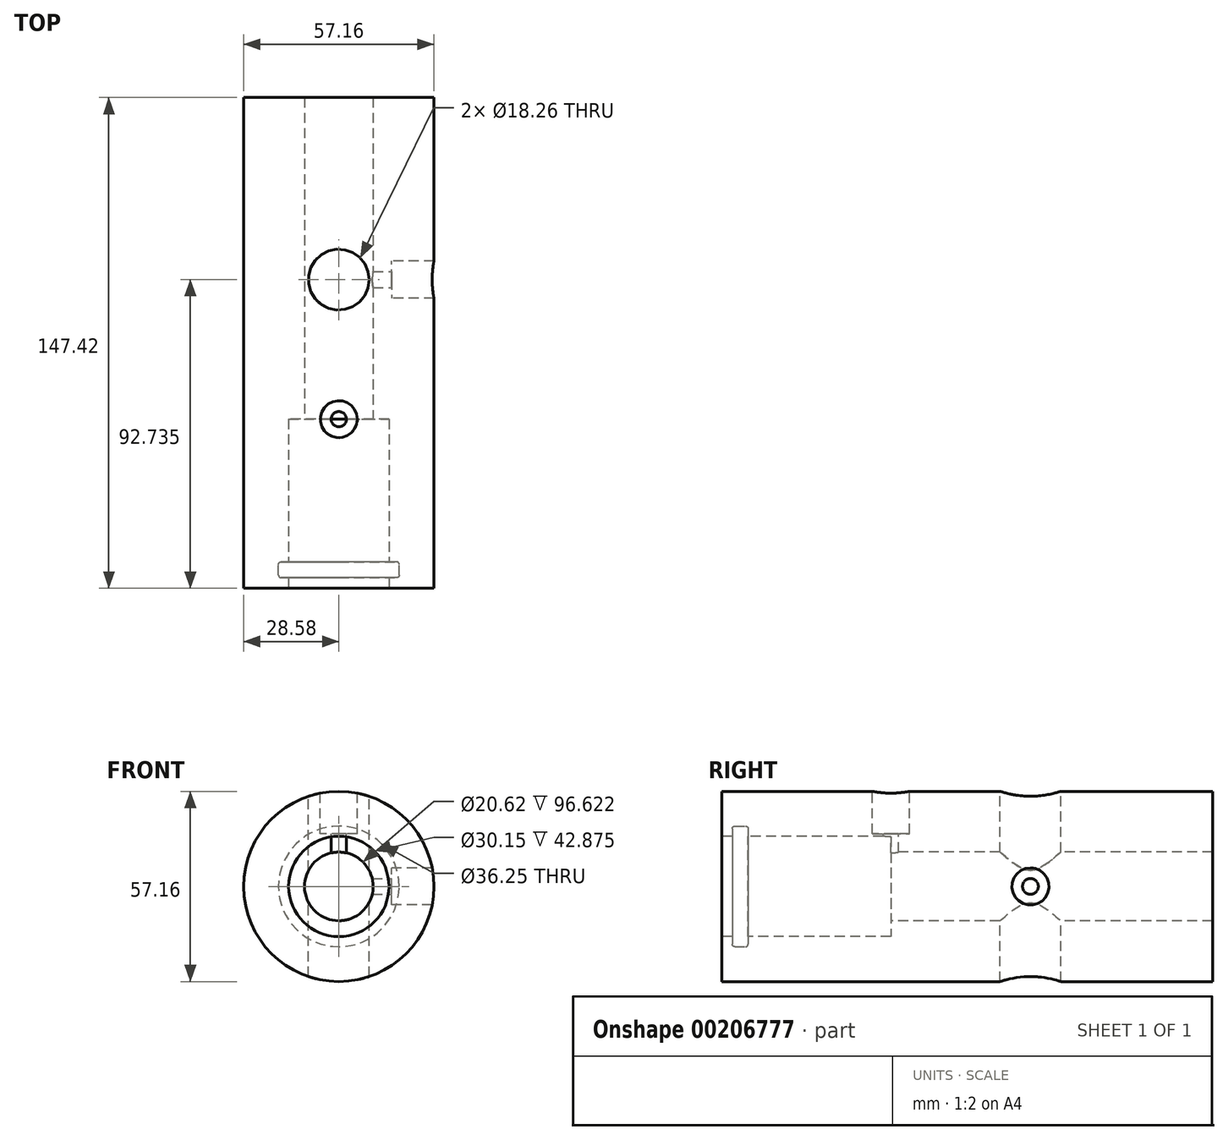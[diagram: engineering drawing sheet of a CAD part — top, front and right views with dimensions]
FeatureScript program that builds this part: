
annotation { "Feature Type Name" : "Feature", "Feature Type Description" : "" }
export const myFeature = defineFeature(function(context is Context, id is Id, definition is map)
    precondition{}
    {
        {
            var Q0;
            Q0=qCreatedBy(makeId("Front.planeOp"),FACE);
            var sketch = newSketch(context, id + "F0", { "sketchPlane" : qUnion([Q0])});
            skCircle(sketch, "E0", {"center": v(0, 0) * mm, "radius": 28.58 * mm});
            skSolve(sketch);
        }
        {
            var Q0;
            Q0=qSketchRegion(id+"F0",true);
            extrude(context, id + "F1", {"entities" : qUnion([Q0]), "oppositeDirection" : true, "depth" : 147.42 * mm});
        }
        {
            var Q0;
            Q0=makeQuery(id+"F1.opExtrude","CAP_FACE",FACE,{"disambiguationData":[OSD([sQuery(id+"F0.wireOp",EDGE,"E0")])],"isStart":true});
            var sketch = newSketch(context, id + "F2", { "sketchPlane" : qUnion([Q0])});
            skCircle(sketch, "E1", {"center": v(0, 0) * mm, "radius": 15.07 * mm});
            skCircle(sketch, "E2", {"center": v(0, 0) * mm, "radius": 10.31 * mm});
            skSolve(sketch);
        }
        {
            var Q0;
            Q0=makeQuery(id+"F2.imprint","IMPRINT",FACE,{"disambiguationData":[TD([[makeQuery(id+"F2.imprint","IMPRINT",EDGE,{"derivedFrom":sQuery(id+"F2.wireOp",EDGE,"E2")}),1.0]])]});
            extrude(context, id + "F3", {"entities" : qUnion([Q0]), "operationType" : NewBodyOperationType.REMOVE, "endBound" : BoundingType.THROUGH_ALL, "oppositeDirection" : true, "depth" : 25.4 * mm});
        }
        {
            var Q0;
            Q0=qSketchRegion(id+"F2",true);
            extrude(context, id + "F4", {"entities" : qUnion([Q0]), "operationType" : NewBodyOperationType.REMOVE, "oppositeDirection" : true, "depth" : 50.8 * mm});
        }
        {
            var Q0;
            Q0=qCreatedBy(makeId("Top.planeOp"),FACE);
            cPlane(context, id + "F5", {"entities" : qUnion([Q0]), "cplaneType" : CPlaneType.OFFSET, "offset" : 28.57 * mm, "width" : 152.4 * mm, "height" : 152.4 * mm});
        }
        {
            var Q0;
            Q0=qCreatedBy(id+"F5.planeOp",FACE);
            var sketch = newSketch(context, id + "F6", { "sketchPlane" : qUnion([Q0])});
            skCircle(sketch, "E3", {"center": v(0, 92.74) * mm, "radius": 9.13 * mm});
            skSolve(sketch);
        }
        {
            var Q0;
            Q0=qSketchRegion(id+"F6",true);
            var Q1;
            Q1=makeQuery(id+"F3.boolean.opBoolean","COPY",FACE,{"derivedFrom":makeQuery(id+"F3.opExtrude","SWEPT_FACE",FACE,{"disambiguationData":[OSD([sQuery(id+"F2.wireOp",EDGE,"E2")])]})});
            extrude(context, id + "F7", {"entities" : qUnion([Q0]), "operationType" : NewBodyOperationType.REMOVE, "endBound" : BoundingType.THROUGH_ALL, "oppositeDirection" : true, "endBoundEntityFace" : qUnion([Q1]), "depth" : 19.05 * mm});
        }
        {
            var Q0;
            Q0=qCreatedBy(makeId("Right.planeOp"),FACE);
            var sketch = newSketch(context, id + "F8", { "sketchPlane" : qUnion([Q0])});
            skLineSegment(sketch, "E4", {"start": v(0, 0) * mm, "end": v(50.8, 0) * mm, "construction": true});
            skLineSegment(sketch, "E5.bottom", {"start": v(3.17, 18.12) * mm, "end": v(7.92, 18.12) * mm});
            skLineSegment(sketch, "E5.top", {"start": v(3.17, 15.07) * mm, "end": v(7.92, 15.07) * mm});
            skLineSegment(sketch, "E5.left", {"start": v(3.17, 15.07) * mm, "end": v(3.17, 18.12) * mm});
            skLineSegment(sketch, "E5.right", {"start": v(7.92, 15.07) * mm, "end": v(7.92, 18.12) * mm});
            skSolve(sketch);
        }
        {
            var Q0;
            Q0=qSketchRegion(id+"F8",true);
            var Q1;
            Q1=sQuery(id+"F8.wireOp",EDGE,"E4");
            revolve(context, id + "F9", {"operationType" : NewBodyOperationType.REMOVE, "entities" : qUnion([Q0]), "axis" : qUnion([Q1]), "revolveType" : RevolveType.FULL, "oppositeDirection" : true});
        }
        {
            var Q0;
            Q0=qCreatedBy(id+"F5.planeOp",FACE);
            var sketch = newSketch(context, id + "F10", { "sketchPlane" : qUnion([Q0])});
            skCircle(sketch, "E6", {"center": v(0, 50.8) * mm, "radius": 5.56 * mm});
            skCircle(sketch, "E7", {"center": v(0, 50.8) * mm, "radius": 2.29 * mm});
            skSolve(sketch);
        }
        {
            var Q0;
            Q0=makeQuery(id+"F10.imprint","IMPRINT",FACE,{"disambiguationData":[TD([[makeQuery(id+"F10.imprint","IMPRINT",EDGE,{"derivedFrom":sQuery(id+"F10.wireOp",EDGE,"E7")}),1.0]])]});
            extrude(context, id + "F11", {"entities" : qUnion([Q0]), "operationType" : NewBodyOperationType.REMOVE, "endBound" : BoundingType.UP_TO_NEXT, "oppositeDirection" : true, "depth" : 25.4 * mm});
        }
        {
            var Q0;
            Q0=qSketchRegion(id+"F10",true);
            extrude(context, id + "F12", {"entities" : qUnion([Q0]), "operationType" : NewBodyOperationType.REMOVE, "oppositeDirection" : true, "depth" : 12.7 * mm});
        }
        {
            var Q0;
            Q0=qCreatedBy(makeId("Right.planeOp"),FACE);
            var sketch = newSketch(context, id + "F13", { "sketchPlane" : qUnion([Q0])});
            skLineSegment(sketch, "E8", {"start": v(92.74, 28.58) * mm, "end": v(92.74, 0) * mm, "construction": true});
            skCircle(sketch, "E9", {"center": v(92.74, 0) * mm, "radius": 5.56 * mm});
            skSolve(sketch);
        }
        {
            var Q0;
            Q0 = qSketchRegion(id + "F13", true);
            var Q1;
            Q1=makeQuery(id+"F1.opExtrude","SWEPT_FACE",FACE,{"disambiguationData":[OSD([sQuery(id+"F0.wireOp",EDGE,"E0")])]});
            extrude(context, id + "F14", {"entities" : qUnion([Q0]), "operationType" : NewBodyOperationType.REMOVE, "endBound" : BoundingType.UP_TO_SURFACE, "endBoundEntityFace" : qUnion([Q1]), "depth" : 25.4 * mm, "hasSecondDirection" : true, "secondDirectionOppositeDirection" : false, "secondDirectionDepth" : 15.88 * mm});
        }
        {
            var Q0;
            Q0=makeQuery(id+"F14.boolean.opBoolean","COPY",FACE,{"derivedFrom":makeQuery(id+"F14.opExtrude","CAP_FACE",FACE,{"disambiguationData":[OSD([sQuery(id+"F13.wireOp",EDGE,"E9")])],"isStart":true})});
            var sketch = newSketch(context, id + "F15", { "sketchPlane" : qUnion([Q0])});
            skCircle(sketch, "E10", {"center": v(92.74, 0) * mm, "radius": 2.38 * mm});
            skSolve(sketch);
        }
        {
            var Q0;
            Q0 = qSketchRegion(id + "F15", true);
            extrude(context, id + "F16", {"entities" : qUnion([Q0]), "operationType" : NewBodyOperationType.REMOVE, "endBound" : BoundingType.UP_TO_NEXT, "oppositeDirection" : true, "depth" : 25.4 * mm});
        }
        {
            var Q0;
            Q0=makeQuery(id+"F9.boolean.opBoolean","COPY",EDGE,{"derivedFrom":makeQuery(id+"F9.opRevolve","SWEPT_EDGE",EDGE,{"disambiguationData":[OSD([sQuery(id+"F8.wireOp",EDGE,"E5.bottom"),sQuery(id+"F8.wireOp",EDGE,"E5.left")])]})});
            var Q1;
            Q1=makeQuery(id+"F9.boolean.opBoolean","COPY",EDGE,{"derivedFrom":makeQuery(id+"F9.opRevolve","SWEPT_EDGE",EDGE,{"disambiguationData":[OSD([sQuery(id+"F8.wireOp",EDGE,"E5.bottom"),sQuery(id+"F8.wireOp",EDGE,"E5.right")])]})});
            fillet(context, id + "F17", {"entities" : qUnion([Q0, Q1]), "radius" : 0.76 * mm, "tangentPropagation" : true, "allowEdgeOverflow" : false});
        }
        {
            var Q0;
            Q0=makeQuery(id+"F9.boolean.opBoolean","COPY",EDGE,{"derivedFrom":makeQuery(id+"F9.opRevolve","SWEPT_EDGE",EDGE,{"disambiguationData":[OSD([sQuery(id+"F8.wireOp",EDGE,"E5.top"),sQuery(id+"F8.wireOp",EDGE,"E5.right")])]})});
            var Q1;
            Q1=makeQuery(id+"F9.boolean.opBoolean","COPY",EDGE,{"derivedFrom":makeQuery(id+"F9.opRevolve","SWEPT_EDGE",EDGE,{"disambiguationData":[OSD([sQuery(id+"F8.wireOp",EDGE,"E5.top"),sQuery(id+"F8.wireOp",EDGE,"E5.left")])]})});
            fillet(context, id + "F18", {"entities" : qUnion([Q0, Q1]), "radius" : 0.13 * mm, "tangentPropagation" : true, "allowEdgeOverflow" : false});
        }
    });
